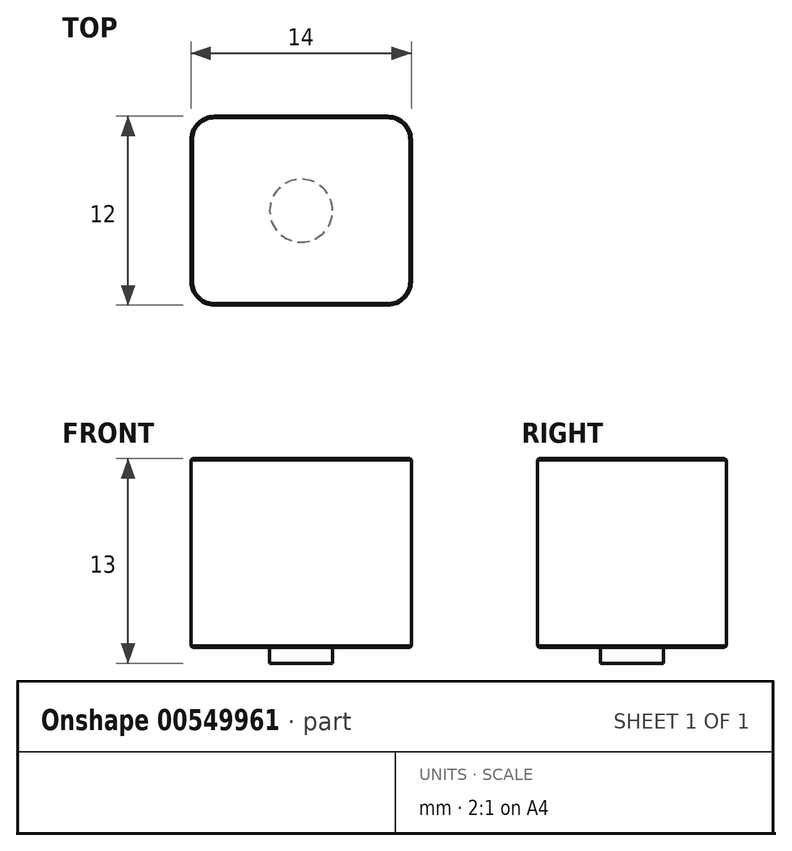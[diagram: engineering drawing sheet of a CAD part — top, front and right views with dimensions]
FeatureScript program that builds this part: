
annotation { "Feature Type Name" : "Feature", "Feature Type Description" : "" }
export const myFeature = defineFeature(function(context is Context, id is Id, definition is map)
    precondition{}
    {
        {
            var Q0;
            Q0=qCreatedBy(makeId("Top.planeOp"),FACE);
            var sketch = newSketch(context, id + "F0", { "sketchPlane" : qUnion([Q0])});
            skLineSegment(sketch, "E0.bottom", {"start": v(5.5, -6) * mm, "end": v(-5.5, -6) * mm});
            skLineSegment(sketch, "E0.top", {"start": v(5.5, 6) * mm, "end": v(-5.5, 6) * mm});
            skLineSegment(sketch, "E0.left", {"start": v(7, -4.5) * mm, "end": v(7, 4.5) * mm});
            skLineSegment(sketch, "E0.right", {"start": v(-7, -4.5) * mm, "end": v(-7, 4.5) * mm});
            skPoint(sketch, "E0.middle", {"position": v(0, 0) * mm});
            skPoint(sketch, "E1.visualSharp", {"position": v(-7, -6) * mm});
            skArc(sketch, "E1.filletArc", {"start": v(-7, -4.5) * mm, "mid": v(-6.56, -5.56) * mm, "end": v(-5.5, -6) * mm});
            skPoint(sketch, "E2.visualSharp", {"position": v(-7, 6) * mm});
            skArc(sketch, "E2.filletArc", {"start": v(-5.5, 6) * mm, "mid": v(-6.56, 5.56) * mm, "end": v(-7, 4.5) * mm});
            skPoint(sketch, "E3.visualSharp", {"position": v(7, 6) * mm});
            skArc(sketch, "E3.filletArc", {"start": v(7, 4.5) * mm, "mid": v(6.56, 5.56) * mm, "end": v(5.5, 6) * mm});
            skPoint(sketch, "E4.visualSharp", {"position": v(7, -6) * mm});
            skArc(sketch, "E4.filletArc", {"start": v(5.5, -6) * mm, "mid": v(6.56, -5.56) * mm, "end": v(7, -4.5) * mm});
            skSolve(sketch);
        }
        {
            var Q0;
            Q0=makeQuery(id+"F0.imprint","IMPRINT",FACE,{"disambiguationData":[TD([[makeQuery(id+"F0.imprint","IMPRINT",EDGE,{"derivedFrom":sQuery(id+"F0.wireOp",EDGE,"E0.bottom")}),-1.0]])]});
            extrude(context, id + "F1", {"entities" : qUnion([Q0]), "depth" : 12 * mm, "offsetDistance" : 25 * mm});
        }
        {
            var Q0;
            Q0=makeQuery(id+"F1.opExtrude","CAP_FACE",FACE,{"disambiguationData":[OSD([sQuery(id+"F0.wireOp",EDGE,"E0.bottom"),sQuery(id+"F0.wireOp",EDGE,"E0.top"),sQuery(id+"F0.wireOp",EDGE,"E0.left"),sQuery(id+"F0.wireOp",EDGE,"E0.right"),sQuery(id+"F0.wireOp",EDGE,"E1.filletArc"),sQuery(id+"F0.wireOp",EDGE,"E2.filletArc"),sQuery(id+"F0.wireOp",EDGE,"E3.filletArc"),sQuery(id+"F0.wireOp",EDGE,"E4.filletArc")])],"isStart":false});
            var Q1;
            Q1=makeQuery(id+"F1.opExtrude","CAP_FACE",FACE,{"disambiguationData":[OSD([sQuery(id+"F0.wireOp",EDGE,"E0.bottom"),sQuery(id+"F0.wireOp",EDGE,"E0.top"),sQuery(id+"F0.wireOp",EDGE,"E0.left"),sQuery(id+"F0.wireOp",EDGE,"E0.right"),sQuery(id+"F0.wireOp",EDGE,"E1.filletArc"),sQuery(id+"F0.wireOp",EDGE,"E2.filletArc"),sQuery(id+"F0.wireOp",EDGE,"E3.filletArc"),sQuery(id+"F0.wireOp",EDGE,"E4.filletArc")])],"isStart":true});
            chamfer(context, id + "F2", {"entities" : qUnion([Q0, Q1]), "width" : 0.1 * mm, "tangentPropagation" : true});
        }
        {
            var Q0;
            Q0=makeQuery(id+"F1.opExtrude","CAP_FACE",FACE,{"disambiguationData":[OSD([sQuery(id+"F0.wireOp",EDGE,"E0.bottom"),sQuery(id+"F0.wireOp",EDGE,"E0.top"),sQuery(id+"F0.wireOp",EDGE,"E0.left"),sQuery(id+"F0.wireOp",EDGE,"E0.right"),sQuery(id+"F0.wireOp",EDGE,"E1.filletArc"),sQuery(id+"F0.wireOp",EDGE,"E2.filletArc"),sQuery(id+"F0.wireOp",EDGE,"E3.filletArc"),sQuery(id+"F0.wireOp",EDGE,"E4.filletArc")])],"isStart":true});
            var sketch = newSketch(context, id + "F3", { "sketchPlane" : qUnion([Q0])});
            skCircle(sketch, "E5", {"center": v(0, 0) * mm, "radius": 2 * mm});
            skSolve(sketch);
        }
        {
            var Q0;
            Q0=makeQuery(id+"F3.imprint","IMPRINT",FACE,{"disambiguationData":[TD([[makeQuery(id+"F3.imprint","IMPRINT",EDGE,{"derivedFrom":sQuery(id+"F3.wireOp",EDGE,"E5")}),1.0]])]});
            extrude(context, id + "F4", {"entities" : qUnion([Q0]), "operationType" : NewBodyOperationType.ADD, "depth" : 1 * mm, "offsetDistance" : 25 * mm});
        }
    });
